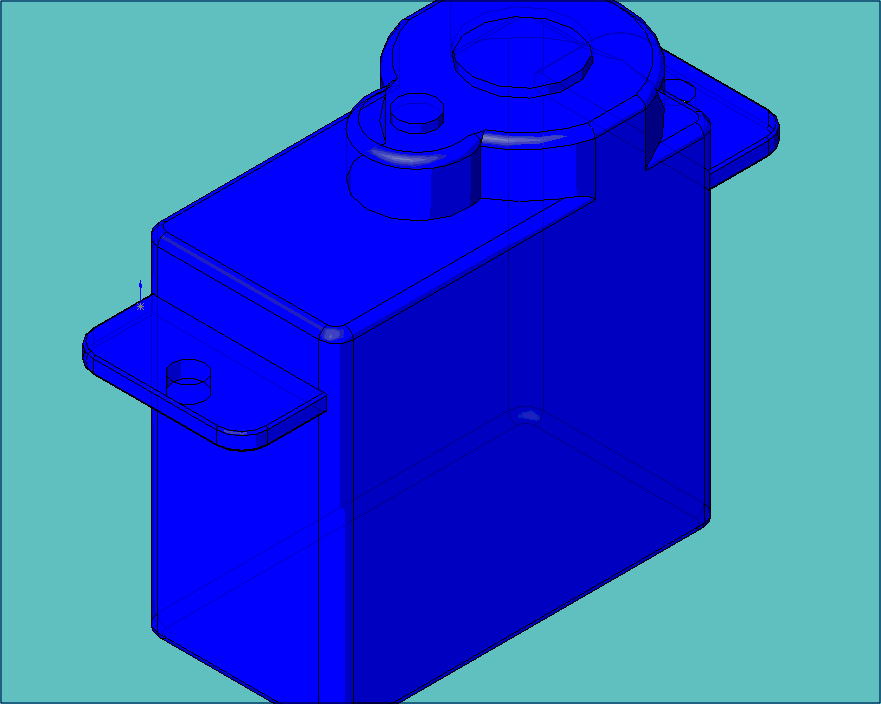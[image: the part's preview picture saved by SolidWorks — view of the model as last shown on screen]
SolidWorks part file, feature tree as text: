
SOLIDWORKS PART (.sldprt)
format: sldprt  version: not decoded by parser v0  size: 441,856 bytes
history: native  units: mm
features: sketch x4, fillet x4, extrude x3, material x1, cut_extrude x1 (+14 scaffold rows collapsed)
feature tree (27):
  scaffold x14  (default folders/planes/origin — collapsed)
  material  "Material <not specified>"
  sketch  "Sketch1"  dims[D1=0.9906mm D2=22.7076mm D3=20.7264mm D4=16.6624mm D5=32.5628mm]
  extrude  "Extrude1"  Depth=11.5316mm
  sketch  "Sketch3"  dims[c1.D1=1.524mm c1.D3=1.905mm c1.D4=1.905mm c1.D2=10.287mm c2.D4=1.9939mm]
  cut_extrude  "Cut-Extrude2"  [1 undecoded]
  sketch  "Sketch4"  dims[D1=11.9126mm D3=5.9182mm D2=15.1384mm]
  extrude  "Extrude2"  Depth=3.1496mm
  sketch  "Sketch5"  dims[D1=2.286mm D2=5.9182mm]
  extrude  "Extrude3"  Depth=0.508mm
  fillet  "Fillet1"  Radius=1.016mm
  fillet  "Fillet2"  Radius=0.508mm
  fillet  "Fillet3"  Radius=0.508mm
  fillet  "Fillet4"  Radius=0.127mm
decode coverage: 11 of 12 modeling features carry decoded parameters
note: 1 parameter value undecoded
note: suppression state not decoded; provenance and decode notes live in map.json
